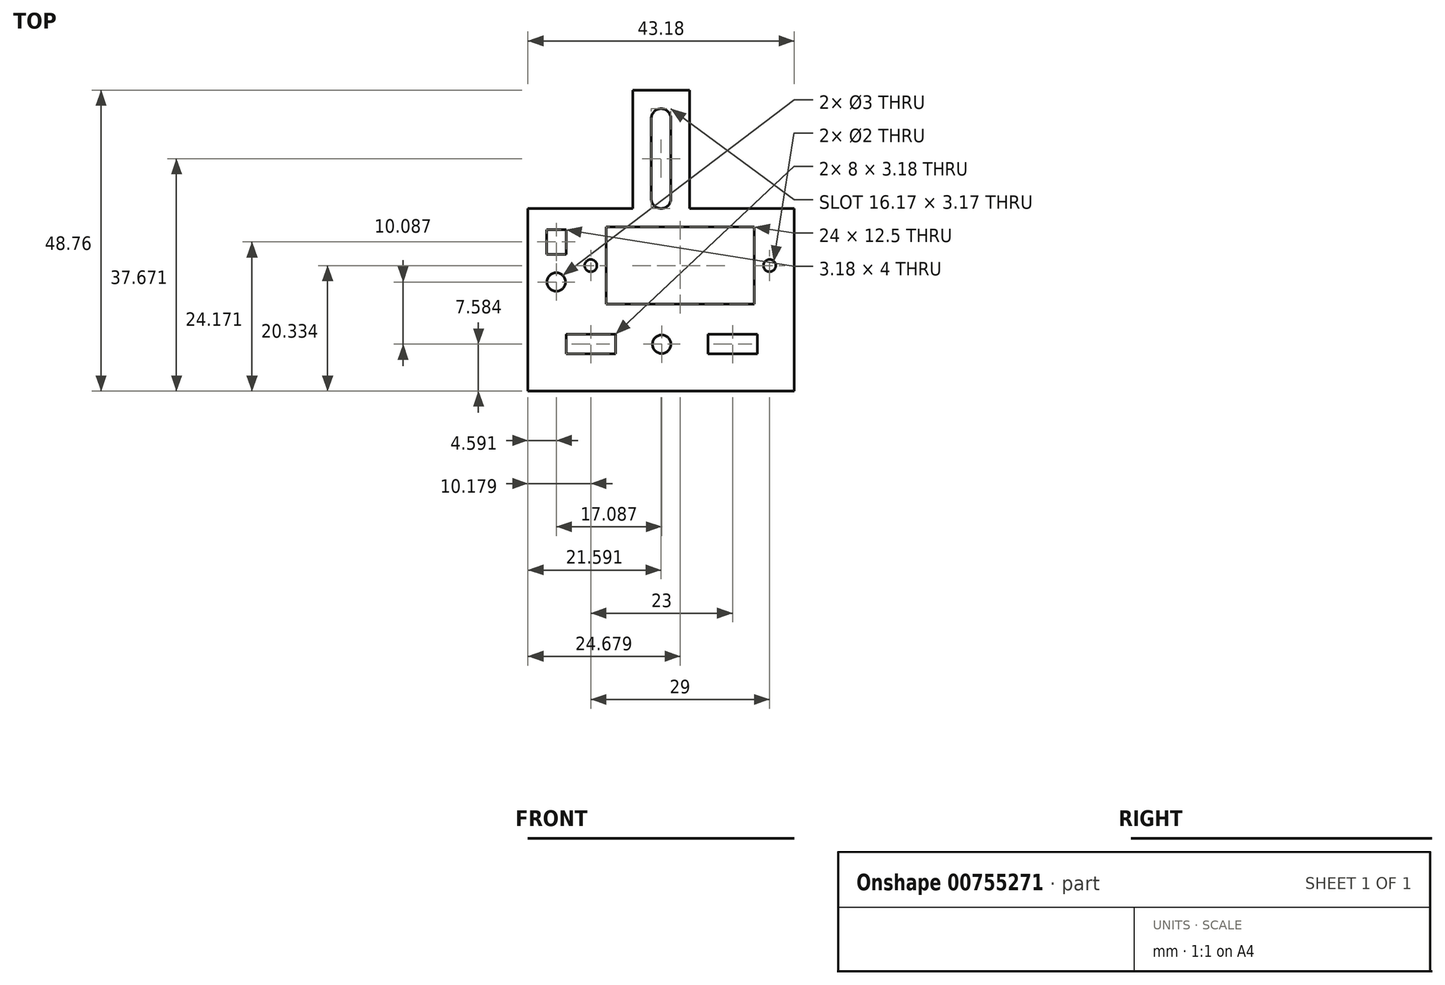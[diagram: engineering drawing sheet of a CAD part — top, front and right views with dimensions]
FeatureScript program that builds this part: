
annotation { "Feature Type Name" : "Feature", "Feature Type Description" : "" }
export const myFeature = defineFeature(function(context is Context, id is Id, definition is map)
    precondition{}
    {
        {
            var Q0;
            Q0=qCreatedBy(makeId("Top.planeOp"),FACE);
            var sketch = newSketch(context, id + "F0", { "sketchPlane" : qUnion([Q0])});
            skArc(sketch, "E0", {"start": v(-10.93, 15.52) * mm, "mid": v(-12.52, 17.1) * mm, "end": v(-14.1, 15.52) * mm});
            skArc(sketch, "E1", {"start": v(-14.1, 2.52) * mm, "mid": v(-12.52, 0.93) * mm, "end": v(-10.93, 2.52) * mm});
            skLineSegment(sketch, "E2", {"start": v(-14.1, 15.52) * mm, "end": v(-14.1, 2.52) * mm});
            skLineSegment(sketch, "E3.MirrorCS", {"start": v(-10.93, 15.52) * mm, "end": v(-10.93, 2.52) * mm});
            skLineSegment(sketch, "E4.bottom", {"start": v(-21.43, -2.07) * mm, "end": v(2.57, -2.07) * mm});
            skLineSegment(sketch, "E4.top", {"start": v(-21.43, -14.57) * mm, "end": v(2.57, -14.57) * mm});
            skLineSegment(sketch, "E4.left", {"start": v(-21.43, -2.07) * mm, "end": v(-21.43, -14.57) * mm});
            skLineSegment(sketch, "E4.right", {"start": v(2.57, -2.07) * mm, "end": v(2.57, -14.57) * mm});
            skPoint(sketch, "E4.middle", {"position": v(-9.43, -8.32) * mm});
            skCircle(sketch, "E5", {"center": v(5.07, -8.32) * mm, "radius": 1 * mm});
            skCircle(sketch, "E6.MirrorC", {"center": v(-23.93, -8.32) * mm, "radius": 1 * mm});
            skCircle(sketch, "E7", {"center": v(-29.52, -10.98) * mm, "radius": 1.5 * mm});
            skLineSegment(sketch, "E8.bottom", {"start": v(-31.1, -2.48) * mm, "end": v(-27.93, -2.48) * mm});
            skLineSegment(sketch, "E8.top", {"start": v(-31.1, -6.48) * mm, "end": v(-27.93, -6.48) * mm});
            skLineSegment(sketch, "E8.left", {"start": v(-31.1, -2.48) * mm, "end": v(-31.1, -6.48) * mm});
            skLineSegment(sketch, "E8.right", {"start": v(-27.93, -2.48) * mm, "end": v(-27.93, -6.48) * mm});
            skPoint(sketch, "E8.middle", {"position": v(-29.52, -4.48) * mm});
            skCircle(sketch, "E9", {"center": v(-12.43, -21.07) * mm, "radius": 1.5 * mm});
            skLineSegment(sketch, "E10.bottom", {"start": v(-4.93, -19.48) * mm, "end": v(3.07, -19.48) * mm});
            skLineSegment(sketch, "E10.top", {"start": v(-4.93, -22.65) * mm, "end": v(3.07, -22.65) * mm});
            skLineSegment(sketch, "E10.left", {"start": v(-4.93, -19.48) * mm, "end": v(-4.93, -22.65) * mm});
            skLineSegment(sketch, "E10.right", {"start": v(3.07, -19.48) * mm, "end": v(3.07, -22.65) * mm});
            skPoint(sketch, "E10.middle", {"position": v(-0.93, -21.07) * mm});
            skLineSegment(sketch, "E11.MirrorCS", {"start": v(-19.93, -19.48) * mm, "end": v(-19.93, -22.65) * mm});
            skLineSegment(sketch, "E12.MirrorCS", {"start": v(-19.93, -19.48) * mm, "end": v(-27.93, -19.48) * mm});
            skLineSegment(sketch, "E13.MirrorCS", {"start": v(-19.93, -22.65) * mm, "end": v(-27.93, -22.65) * mm});
            skLineSegment(sketch, "E14.MirrorCS", {"start": v(-27.93, -19.48) * mm, "end": v(-27.93, -22.65) * mm});
            skLineSegment(sketch, "E15.bottom", {"start": v(-34.1, -28.65) * mm, "end": v(9.07, -28.65) * mm});
            skLineSegment(sketch, "E15.top", {"start": v(-34.1, 0.93) * mm, "end": v(-17.1, 0.93) * mm});
            skLineSegment(sketch, "E15.left", {"start": v(-34.1, -28.65) * mm, "end": v(-34.1, 0.93) * mm});
            skLineSegment(sketch, "E15.right", {"start": v(9.07, -28.65) * mm, "end": v(9.07, 0.93) * mm});
            skLineSegment(sketch, "E16.top", {"start": v(-17.1, 20.1) * mm, "end": v(-7.93, 20.1) * mm});
            skLineSegment(sketch, "E16.left", {"start": v(-17.1, 0.93) * mm, "end": v(-17.1, 20.1) * mm});
            skLineSegment(sketch, "E16.right", {"start": v(-7.93, 0.93) * mm, "end": v(-7.93, 20.1) * mm});
            skLineSegment(sketch, "E17.trimOffspring", {"start": v(-7.93, 0.93) * mm, "end": v(9.07, 0.93) * mm});
            skPoint(sketch, "E18.end.orphan", {"position": v(-9.43, -2.07) * mm});
            skSolve(sketch);
        }
        {
            var Q0;
            {var subQ1=sQuery(id+"F0.wireOp",EDGE,"E2");Q0=makeQuery(id+"F0.imprint","IMPRINT",FACE,{"disambiguationData":[TD([[makeQuery(id+"F0.imprint","IMPRINT",EDGE,{"derivedFrom":subQ1}),-1.0]])]});}
            var Q1;
            Q1=makeQuery(id+"F0.imprint","IMPRINT",FACE,{"disambiguationData":[TD([[makeQuery(id+"F0.imprint","IMPRINT",EDGE,{"derivedFrom":sQuery(id+"F0.wireOp",EDGE,"E4.top")}),-1.0]])]});
            extrude(context, id + "F1", {"entities" : qUnion([Q0, Q1]), "depth" : 1 / 203.2 * mm, "offsetDistance" : 25 * mm});
        }
    });
